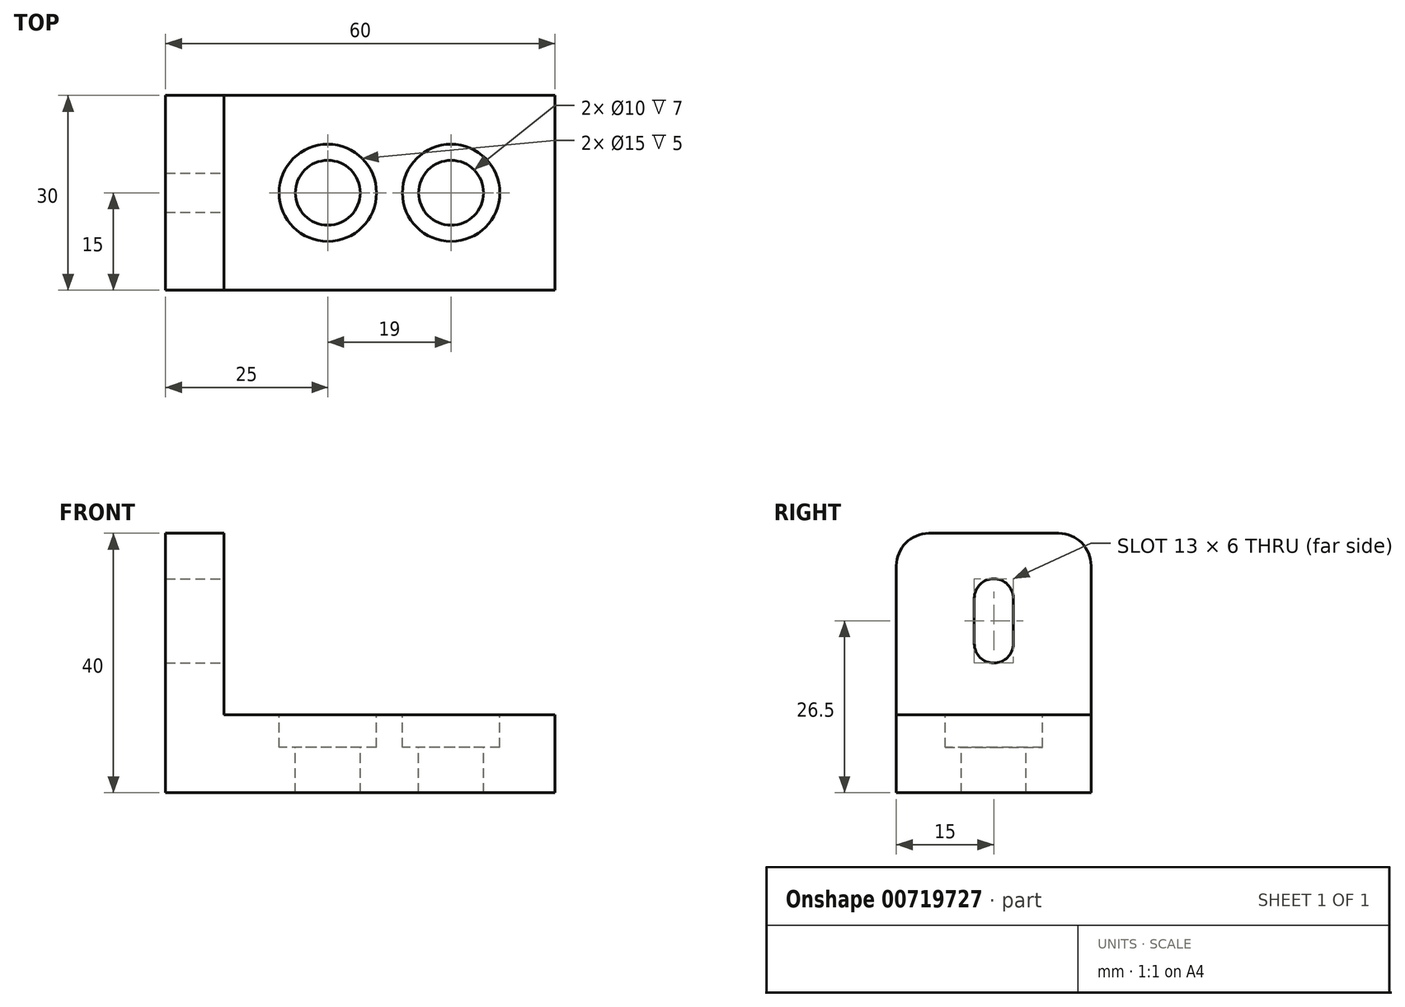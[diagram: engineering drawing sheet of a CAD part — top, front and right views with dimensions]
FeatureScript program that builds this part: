
annotation { "Feature Type Name" : "Feature", "Feature Type Description" : "" }
export const myFeature = defineFeature(function(context is Context, id is Id, definition is map)
    precondition{}
    {
        {
            var Q0;
            Q0=qCreatedBy(makeId("Front.planeOp"),FACE);
            var sketch = newSketch(context, id + "F0", { "sketchPlane" : qUnion([Q0])});
            skLineSegment(sketch, "E0", {"start": v(60, 0) * mm, "end": v(0, 0) * mm});
            skLineSegment(sketch, "E1", {"start": v(0, 0) * mm, "end": v(0, 40) * mm});
            skLineSegment(sketch, "E2", {"start": v(0, 40) * mm, "end": v(9, 40) * mm});
            skLineSegment(sketch, "E3", {"start": v(9, 40) * mm, "end": v(9, 12) * mm});
            skLineSegment(sketch, "E4", {"start": v(9, 12) * mm, "end": v(60, 12) * mm});
            skLineSegment(sketch, "E5", {"start": v(60, 12) * mm, "end": v(60, 0) * mm});
            skSolve(sketch);
        }
        {
            var Q0;
            Q0=makeQuery(id+"F0.imprint","IMPRINT",FACE,{"disambiguationData":[TD([[makeQuery(id+"F0.imprint","IMPRINT",EDGE,{"derivedFrom":sQuery(id+"F0.wireOp",EDGE,"E0")}),-1.0]])]});
            extrude(context, id + "F1", {"entities" : qUnion([Q0]), "depth" : 30 * mm, "offsetDistance" : 25 * mm});
        }
        {
            var Q0;
            Q0=makeQuery(id+"F1.opExtrude","CAP_EDGE",EDGE,{"disambiguationData":[OSD([sQuery(id+"F0.wireOp",EDGE,"E2")])],"isStart":false});
            fillet(context, id + "F2", {"entities" : qUnion([Q0]), "radius" : 5 * mm, "tangentPropagation" : true, "allowEdgeOverflow" : false});
        }
        {
            var Q0;
            Q0=makeQuery(id+"F1.opExtrude","CAP_EDGE",EDGE,{"disambiguationData":[OSD([sQuery(id+"F0.wireOp",EDGE,"E2")])],"isStart":true});
            fillet(context, id + "F3", {"entities" : qUnion([Q0]), "radius" : 5 * mm, "tangentPropagation" : true, "allowEdgeOverflow" : false});
        }
        {
            var Q0;
            Q0=makeQuery(id+"F1.opExtrude","SWEPT_FACE",FACE,{"disambiguationData":[OSD([sQuery(id+"F0.wireOp",EDGE,"E4")])]});
            var sketch = newSketch(context, id + "F4", { "sketchPlane" : qUnion([Q0])});
            skPoint(sketch, "E6", {"position": v(44, -15) * mm});
            skSolve(sketch);
        }
        {
            var Q0;
            {var subQ0=sQuery(id+"F0.wireOp",EDGE,"E4");Q0=makeQuery(id+"F4.imprint","IMPRINT",FACE,{"disambiguationData":[TD([[makeQuery(id+"F4.imprint","IMPRINT",EDGE,{"derivedFrom":makeQuery(id+"F1.opExtrude","CAP_EDGE",EDGE,{"disambiguationData":[OSD([subQ0])],"isStart":true})}),-1.0]])]});}
            var sketch = newSketch(context, id + "F5", { "sketchPlane" : qUnion([Q0])});
            skPoint(sketch, "E7", {"position": v(25, -15) * mm});
            skSolve(sketch);
        }
        {
            var Q0;
            Q0=sQuery(id+"F4.wireOp",VERTEX,"E6");
            var Q1;
            Q1=makeQuery(id+"F1.opExtrude","SWEPT_BODY",BODY,{"disambiguationData":[OSD([sQuery(id+"F0.wireOp",EDGE,"E0"),sQuery(id+"F0.wireOp",EDGE,"E1"),sQuery(id+"F0.wireOp",EDGE,"E2"),sQuery(id+"F0.wireOp",EDGE,"E3"),sQuery(id+"F0.wireOp",EDGE,"E4"),sQuery(id+"F0.wireOp",EDGE,"E5")])]});
            hole(context, id + "F6", {"style" : HoleStyle.C_BORE, "endStyle" : HoleEndStyle.THROUGH, "holeDiameter" : 10 * mm, "cBoreDiameter" : 15 * mm, "cBoreDepth" : 5 * mm, "majorDiameter" : 5 * mm, "isTappedThrough" : true, "tappedDepth" : 12 * mm, "tapClearance" : 3, "locations" : qUnion([Q0]), "scope" : qUnion([Q1])});
        }
        {
            var Q0;
            Q0=sQuery(id+"F5.wireOp",VERTEX,"E7");
            var Q1;
            Q1=makeQuery(id+"F1.opExtrude","SWEPT_BODY",BODY,{"disambiguationData":[OSD([sQuery(id+"F0.wireOp",EDGE,"E0"),sQuery(id+"F0.wireOp",EDGE,"E1"),sQuery(id+"F0.wireOp",EDGE,"E2"),sQuery(id+"F0.wireOp",EDGE,"E3"),sQuery(id+"F0.wireOp",EDGE,"E4"),sQuery(id+"F0.wireOp",EDGE,"E5")])]});
            hole(context, id + "F7", {"style" : HoleStyle.C_BORE, "endStyle" : HoleEndStyle.THROUGH, "holeDiameter" : 10 * mm, "cBoreDiameter" : 15 * mm, "cBoreDepth" : 5 * mm, "majorDiameter" : 5 * mm, "isTappedThrough" : true, "tappedDepth" : 12 * mm, "tapClearance" : 3, "locations" : qUnion([Q0]), "scope" : qUnion([Q1])});
        }
        {
            var Q0;
            Q0=makeQuery(id+"F1.opExtrude","SWEPT_FACE",FACE,{"disambiguationData":[OSD([sQuery(id+"F0.wireOp",EDGE,"E3")])]});
            var sketch = newSketch(context, id + "F8", { "sketchPlane" : qUnion([Q0])});
            skLineSegment(sketch, "E8.left", {"start": v(-18, 30) * mm, "end": v(-18, 23) * mm});
            skLineSegment(sketch, "E8.right", {"start": v(-12, 30) * mm, "end": v(-12, 23) * mm});
            skArc(sketch, "E9", {"start": v(-12, 30) * mm, "mid": v(-15, 33) * mm, "end": v(-18, 30) * mm});
            skArc(sketch, "E10", {"start": v(-18, 23) * mm, "mid": v(-15, 20) * mm, "end": v(-12, 23) * mm});
            skSolve(sketch);
        }
        {
            var Q0;
            {var subQ0=sQuery(id+"F8.wireOp",EDGE,"E9");Q0=makeQuery(id+"F8.imprint","IMPRINT",FACE,{"disambiguationData":[TD([[makeQuery(id+"F8.imprint","IMPRINT",EDGE,{"derivedFrom":subQ0}),1.0]])]});}
            extrude(context, id + "F9", {"entities" : qUnion([Q0]), "operationType" : NewBodyOperationType.REMOVE, "endBound" : BoundingType.THROUGH_ALL, "oppositeDirection" : true, "depth" : 25 * mm, "offsetDistance" : 25 * mm});
        }
    });
